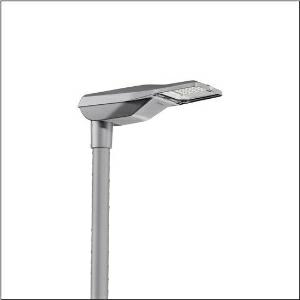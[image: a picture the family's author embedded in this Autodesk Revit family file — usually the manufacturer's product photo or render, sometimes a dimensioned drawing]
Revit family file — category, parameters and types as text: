
# Revit family: streetlight_sl_21_iq_micro___st1_0a_5xe1d21d08cb_1078
name_source: partatom
category: Lighting Fixtures
units: mm (PartAtom-declared; Revit-internal decimal feet)

## family parameters
Cut with Voids When Loaded = No
Host = Face
Light Source = No
Part Type = Normal
Room Calculation Point = No
Round Connector Dimension = Use Diameter
Shared = No

## types (1)
- --- (1 x LED, 2380 lm, 19.4 W, 2200K)
    Apparent Load = 19 VA
    CIE Flux Codes = 37 72 97 100 100
    Color Rendering = 70
    Color Temperature = 2200K
    Default Elevation = 1800 mm
    Description = Streetlight SL 21 iQ micro, mast luminaire, primary light control with lens, of PMMA, primary optical cover: cover, of toughened safety glass, transparent, light distribution: ST1.0a, light emission: direct distribution, primary light characteristic: asymmetric, installation type: post-top, side-entry, LED, High Power LED, rated luminous flux: 2.380lm, luminous efficacy: 123lm/W, light colour: 722, colour temperature: 2200K, control gear: iQ-Comfort, control: Auto-Match, Temp-Guard, Lumen-Switch, Night-Set, Smart-Wire, Light-Fading, Desk-Remote (wireless, voltage-free reading and setting of iQ features in the workshop via application-optimized NFC function/RFID function), optimised constant luminous flux control (CLO 2.0), pre-setting: linear dimming characteristic, mains connection: 220..240V, AC, 50/60Hz, start of lifetime: 19W, end of service life: 20W, reduction: 10W, luminaire housing, of diecast aluminium, powder-coated, Siteco® metallic grey (DB 702S), corrosivity category C5 mid according to DIN EN ISO 12944, please order mast flange separately, inclination adjustable: 0°, 5°, 10°, 15°, sealing non-destructively replaceable, multi-level sealing system, length: 528mm, width: 235mm, height: 110mm, mast flange for spigot size: 42mm (side-entry): 5XC10008XM4, 60/48mm (side-entry/post-top): 5XC10108XM2, 76/60mm (side-entry/post-top): 5XC10108XM1, protection rating (complete): IP66, insulation class (complete): insulation class II (safety insulation), certification: CE, ENEC, ENEC+, VDE, impact resistance: IK10, permissible operating ambient temperature for outdoor applications: -40..+50°C, standard-compliant lighting for roads and squares, packaging unit: 1 piece

Light Distribution: ST1.0a
    Height = 110 mm
    Lamp = 1 x LED
    Lamp Light Flux = 2380 lm
    Lamp Power = 19.4 W
    Lamp count = 1
    Length = 528 mm
    Luminous efficacy = 123 lm/W
    Manufacturer = Siteco
    ModVariant = No
    Model = 5XE1D21D08CB
    Number of Poles = 1
    OnlyDefault = Yes
    Power Factor = 1
    Product Name = Streetlight SL 21 iQ micro | ST1.0a
    Product group = mast luminaire | pylon top
    ProductGroupID = 6100
    Protection Class = Protection class II
    Protection Degree = IP 66
    RLX_Detail_Level = 1
    RLX_Emergency_Light_Flux = 0 lm
    RLX_Emergency_Type = 0
    RLX_Emergency_Type_DB = No
    RlxData = <blob elided: 98705 chars, md5=f2b347b9>
    Socket = socket
    Standby Power = 0 W
    System Light Flux = 2380 lm
    System Power = 19 W
    Type Comments = factory setting: luminous flux: 100 % | dim-lin: 254 | 387 mA
    Type Image = l_1006881.jpg
    URL = http://relux.com
    VarID = @adj_160839
    Voltage = 0 V
    Weight = 0.00 kg
    Width = 235 mm

## geometry (parser evidence)
native form markers: Blend x4, Sweep x10
no freeform markers — native parametric forms only
